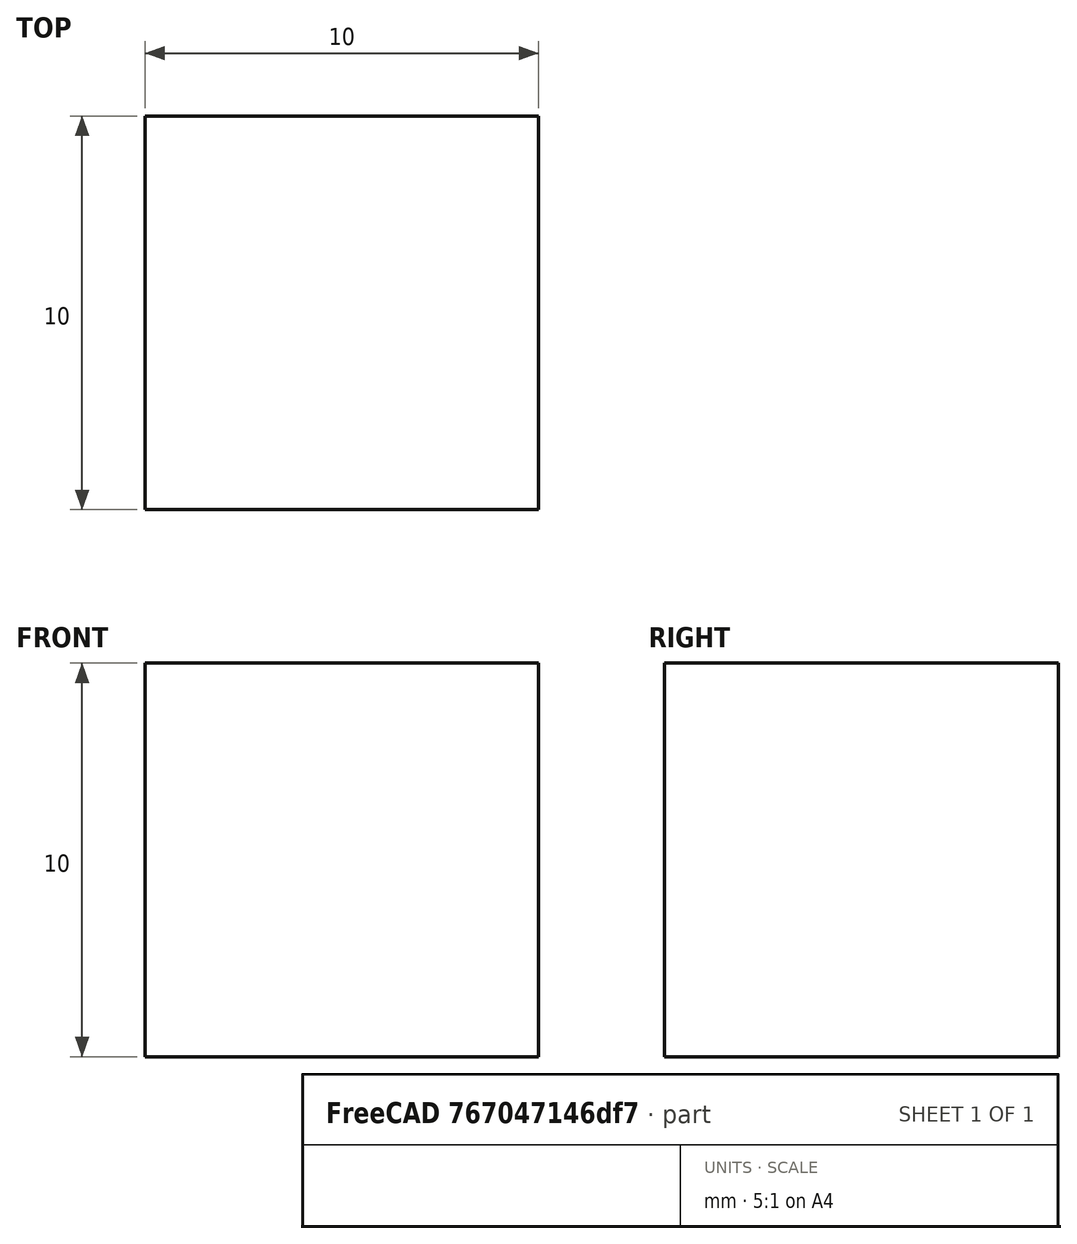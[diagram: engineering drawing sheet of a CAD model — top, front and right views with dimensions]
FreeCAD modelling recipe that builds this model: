
FCSTD DOCUMENT  (FreeCAD 0.21R33694 (Git))
Label: Block_Disp_Control_Example
License: All rights reserved
LicenseURL: http://en.wikipedia.org/wiki/All_rights_reserved
objects: Fem::ConstraintDisplacement×6, Fem::FemMeshObjectPython×2, Part::Box×1, Fem::FemSolverObjectPython×1, App::MaterialObjectPython×1, Fem::FemResultObjectPython×1, Fem::FemAnalysis×1
note: 1 computed .brp shape members not serialized (recipe doc carries the construction recipe); baked Part::Feature solids carry a one-line shape summary decoded from their .brp

FEATURE [Part::Box] Box  label="Cube"
  AttacherType = Attacher::AttachEngine3D
  Height = 10
  Length = 10
  Width = 10
FEATURE [Fem::FemSolverObjectPython] SolverCcxTools  # FEM object (typed FeaturePython)
  AnalysisType = 0
  BeamShellResultOutput3D = false
  BucklingFactors = 1
  EigenmodeHighLimit = 1000000
  EigenmodeLowLimit = 0
  EigenmodesCount = 10
  GeometricalNonlinearity = 0
  IterationsControlParameterCutb = 0.25,0.5,0.75,0.85,,,1.5,
  IterationsControlParameterIter = 4,8,9,200,10,400,,200,,
  IterationsControlParameterTimeUse = false
  IterationsThermoMechMaximum = 2000
  IterationsUserDefinedIncrementations = false
  IterationsUserDefinedTimeStepLength = false
  MaterialNonlinearity = 0
  MatrixSolverType = 0
  SplitInputWriter = false
  ThermoMechSteadyState = true
  TimeEnd = 1
  TimeInitialStep = 0.01
FEATURE [App::MaterialObjectPython] MaterialSolid  # material (typed FeaturePython)
  Category = 0
  Material = AuthorAndLicense=(c) 2013 Juergen Riegel (CC-BY 3.0),CardName=Steel-Generic,Density=7900 kg/m^3,+9 more (map truncated)
FEATURE [Fem::FemMeshObjectPython] FEMMeshGmsh  # FEM object (typed FeaturePython)
  Algorithm2D = 0
  Algorithm3D = 0
  CharacteristicLengthMax = 0
  CharacteristicLengthMin = 10
  CoherenceMesh = true
  ElementDimension = 0
  ElementOrder = 1
  GeometryTolerance = 1e-06
  GroupsOfNodes = false
  HighOrderOptimize = 0
  MeshSizeFromCurvature = 12
  OptimizeNetgen = false
  OptimizeStd = true
  Part = -> Box
  RecombinationAlgorithm = 0
  Recombine3DAll = false
  RecombineAll = false
  SecondOrderLinear = false
FEATURE [Fem::ConstraintDisplacement] ConstraintDisplacement
  NormalDirection = (0,0,-1)
  Normals = (9) [(0,0,-1),(0,0,-1),(0,0,-1),(0,0,-1),(0,0,-1),(0,0,-1),(0,0,-1),(0,0,-1),(0,0,-1)]
  Points = (9) [(0,0,0),(5,0,0),(10,0,0),(0,5,0),(5,5,0),(10,5,0),(0,10,0),(5,10,0),(10,10,0)]
  References = -> [Box]
  hasXFormula = false
  hasYFormula = false
  hasZFormula = false
  rotxFix = false
  rotxFree = true
  rotyFix = false
  rotyFree = true
  rotzFix = false
  rotzFree = true
  useFlowSurfaceForce = false
  xDisplacement = 0
  xFix = false
  xFree = true
  xRotation = 0
  yDisplacement = 0
  yFix = false
  yFree = true
  yRotation = 0
  zDisplacement = 0
  zFix = false
  zFree = false
  zRotation = 0
FEATURE [Fem::ConstraintDisplacement] ConstraintDisplacement001
  NormalDirection = (-1,0,0)
  Normals = (9) [(-1,0,0),(-1,0,0),(-1,0,0),(-1,0,0),(-1,0,0),(-1,0,0),(-1,0,0),(-1,0,0),(-1,0,0)]
  Points = (9) [(0,10,0),(0,10,5),(0,10,10),(0,5,0),(0,5,5),(0,5,10),(0,0,0),(0,0,5),(0,0,10)]
  References = -> [Box]
  hasXFormula = false
  hasYFormula = false
  hasZFormula = false
  rotxFix = false
  rotxFree = true
  rotyFix = false
  rotyFree = true
  rotzFix = false
  rotzFree = true
  useFlowSurfaceForce = false
  xDisplacement = 0
  xFix = false
  xFree = false
  xRotation = 0
  yDisplacement = 0
  yFix = false
  yFree = true
  yRotation = 0
  zDisplacement = 0
  zFix = false
  zFree = true
  zRotation = 0
FEATURE [Fem::ConstraintDisplacement] ConstraintDisplacement002
  NormalDirection = (0,1,0)
  Normals = (9) [(0,1,0),(0,1,0),(0,1,0),(0,1,0),(0,1,0),(0,1,0),(0,1,0),(0,1,0),(0,1,0)]
  Points = (9) [(0,10,0),(0,10,5),(0,10,10),(5,10,0),(5,10,5),(5,10,10),(10,10,0),(10,10,5),(10,10,10)]
  References = -> [Box]
  hasXFormula = false
  hasYFormula = false
  hasZFormula = false
  rotxFix = false
  rotxFree = true
  rotyFix = false
  rotyFree = true
  rotzFix = false
  rotzFree = true
  useFlowSurfaceForce = false
  xDisplacement = 0
  xFix = false
  xFree = true
  xRotation = 0
  yDisplacement = 0
  yFix = false
  yFree = false
  yRotation = 0
  zDisplacement = 0
  zFix = false
  zFree = true
  zRotation = 0
FEATURE [Fem::ConstraintDisplacement] ConstraintDisplacement003
  NormalDirection = (0,0,1)
  Normals = (9) [(0,0,1),(0,0,1),(0,0,1),(0,0,1),(0,0,1),(0,0,1),(0,0,1),(0,0,1),(0,0,1)]
  Points = (9) [(0,0,10),(5,0,10),(10,0,10),(0,5,10),(5,5,10),(10,5,10),(0,10,10),(5,10,10),(10,10,10)]
  References = -> [Box]
  hasXFormula = false
  hasYFormula = false
  hasZFormula = false
  rotxFix = false
  rotxFree = true
  rotyFix = false
  rotyFree = true
  rotzFix = false
  rotzFree = true
  useFlowSurfaceForce = false
  xDisplacement = 0
  xFix = false
  xFree = true
  xRotation = 0
  yDisplacement = 0
  yFix = false
  yFree = true
  yRotation = 0
  zDisplacement = 0.1
  zFix = false
  zFree = false
  zRotation = 0
FEATURE [Fem::ConstraintDisplacement] ConstraintDisplacement004
  NormalDirection = (1,0,0)
  Normals = (9) [(1,0,0),(1,0,0),(1,0,0),(1,0,0),(1,0,0),(1,0,0),(1,0,0),(1,0,0),(1,0,0)]
  Points = (9) [(10,10,0),(10,10,5),(10,10,10),(10,5,0),(10,5,5),(10,5,10),(10,0,0),(10,0,5),(10,0,10)]
  References = -> [Box]
  hasXFormula = false
  hasYFormula = false
  hasZFormula = false
  rotxFix = false
  rotxFree = true
  rotyFix = false
  rotyFree = true
  rotzFix = false
  rotzFree = true
  useFlowSurfaceForce = false
  xDisplacement = 0.01
  xFix = false
  xFree = false
  xRotation = 0
  yDisplacement = 0
  yFix = false
  yFree = true
  yRotation = 0
  zDisplacement = 0
  zFix = false
  zFree = true
  zRotation = 0
FEATURE [Fem::ConstraintDisplacement] ConstraintDisplacement005
  NormalDirection = (0,-1,0)
  Normals = (9) [(0,-1,0),(0,-1,0),(0,-1,0),(0,-1,0),(0,-1,0),(0,-1,0),(0,-1,0),(0,-1,0),(0,-1,0)]
  Points = (9) [(0,0,0),(0,0,5),(0,0,10),(5,0,0),(5,0,5),(5,0,10),(10,0,0),(10,0,5),(10,0,10)]
  References = -> [Box]
  hasXFormula = false
  hasYFormula = false
  hasZFormula = false
  rotxFix = false
  rotxFree = true
  rotyFix = false
  rotyFree = true
  rotzFix = false
  rotzFree = true
  useFlowSurfaceForce = false
  xDisplacement = 0
  xFix = false
  xFree = true
  xRotation = 0
  yDisplacement = -0.01
  yFix = false
  yFree = false
  yRotation = 0
  zDisplacement = 0
  zFix = false
  zFree = true
  zRotation = 0
FEATURE [Fem::FemMeshObjectPython] Result_Mesh_Volume  # FEM object (typed FeaturePython)
FEATURE [Fem::FemResultObjectPython] ResultMechanical  # FEM object (typed FeaturePython)
  CriticalStrainRatio = [1728.93,1728.93,1728.93,1728.93,1728.93,1728.93,1728.93,1728.93,1728.93,1728.93,1728.93,1728.93,1728.93,1728.93,1728.93,1728.93,1728.93,1728.93,1728.93,1728.93,1728.93,1728.93,1728.93,1728.93,1728.93,1728.93,1728.93,1728.93,1728.93,1728.93,+33 more]
  DisplacementLengths = [0.521763,0.0519174,0.519174,0,0.52434,0.0734222,0.521763,0.0519174,0.264728,0.519822,0.259587,0.0259587,0.269771,0.522408,0.264728,0.0580454,0.0580454,0.522408,0.0259587,0.519822,0.260882,0.391322,0.135508,0.389596,0.130441,0.265997,+37 more]
  DisplacementVectors = (63) [(0,-0.0519174,0.519174),(0,-0.0519174,0),(0,0,0.519174),(0,0,0),(0.0519174,-0.0519174,0.519174),(0.0519174,-0.0519174,0),(0.0519174,0,0.519174),+56 more]
  Eigenmode = 0
  EigenmodeFrequency = 0
  Mesh = -> Result_Mesh_Volume
  NodeNumbers = [1,2,3,4,5,6,7,8,9,10,11,12,13,14,15,16,17,18,19,20,21,22,23,24,25,26,27,28,29,30,31,32,33,34,35,36,37,38,39,40,41,42,43,44,45,46,47,48,49,50,51,52,53,54,55,56,57,58,59,60,61,62,63]
  NodeStressXX = [1526.21,1526.21,1526.21,1526.21,1526.21,1526.21,1526.21,1526.21,1526.21,1526.21,1526.21,1526.21,1526.21,1526.21,1526.21,1526.21,1526.21,1526.21,1526.21,1526.21,1526.21,1526.21,1526.21,1526.21,1526.21,1526.21,1526.21,1526.21,1526.21,1526.21,+33 more]
  NodeStressXY = [-2.40836e-12,2.43909e-12,-2.02569e-12,-3.03438e-12,-1.30272e-12,-2.64585e-12,1.82051e-12,3.15597e-12,1.53669e-14,-2.21702e-12,-2.53003e-12,-2.97645e-13,-1.97428e-12,2.58896e-13,2.48824e-12,2.55062e-13,-1.03377e-13,-1.85554e-12,6.0794e-14,+44 more]
  NodeStressXZ = [-1.35346e-11,-2.67087e-12,5.81377e-12,-6.79306e-12,8.92134e-12,9.37934e-13,-6.41394e-12,1.11667e-11,-8.10273e-12,-3.86041e-12,-4.89641e-13,-4.73196e-12,4.92964e-12,1.2537e-12,2.37636e-12,6.0523e-12,-8.66469e-13,-2.30662e-12,2.1868e-12,+44 more]
  NodeStressYY = [1526.21,1526.21,1526.21,1526.21,1526.21,1526.21,1526.21,1526.21,1526.21,1526.21,1526.21,1526.21,1526.21,1526.21,1526.21,1526.21,1526.21,1526.21,1526.21,1526.21,1526.21,1526.21,1526.21,1526.21,1526.21,1526.21,1526.21,1526.21,1526.21,1526.21,+33 more]
  NodeStressYZ = [-1.56677e-11,-2.48802e-11,-1.50031e-11,-2.09902e-11,-3.2508e-11,-4.68106e-12,-1.52833e-11,1.36869e-13,-2.0274e-11,-1.53354e-11,-1.79967e-11,-2.29352e-11,-1.85945e-11,-2.38956e-11,-7.5732e-12,-2.2721e-12,-1.47806e-11,-2.40879e-11,+45 more]
  NodeStressZZ = [100,100,100,100,100,100,100,100,100,100,100,100,100,100,100,100,100,100,100,100,100,100,100,100,100,100,100,100,100,100,100,100,100,100,100,100,100,100,100,100,100,100,100,100,100,100,100,100,100,100,100,100,100,100,100,100,100,100,100,100,+3 more]
  Peeq = [0.00928729,0.00928729,0.00928729,0.00928729,0.00928729,0.00928729,0.00928729,0.00928729,0.00928729,0.00928729,0.00928729,0.00928729,0.00928729,0.00928729,0.00928729,0.00928729,0.00928729,0.00928729,0.00928729,0.00928729,0.00928729,+42 more]
  ResultType = Fem::ResultMechanical
  Stats = [0,0.0519174,-0.0519174,0,0,0.519174,0,0.52434,1426.21,1426.21,0,0,0,0,0,0,0,0,0.00928729,0.00928729,1728.93,1728.93,0,0,0,0]
  Temperature = [1728.93,1728.93,1728.93,1728.93,1728.93,1728.93,1728.93,1728.93,1728.93,1728.93,1728.93,1728.93,1728.93,1728.93,1728.93,1728.93,1728.93,1728.93,1728.93,1728.93,1728.93,1728.93,1728.93,1728.93,1728.93,1728.93,1728.93,1728.93,1728.93,1728.93,+33 more]
  Time = 0
  vonMises = [1426.21,1426.21,1426.21,1426.21,1426.21,1426.21,1426.21,1426.21,1426.21,1426.21,1426.21,1426.21,1426.21,1426.21,1426.21,1426.21,1426.21,1426.21,1426.21,1426.21,1426.21,1426.21,1426.21,1426.21,1426.21,1426.21,1426.21,1426.21,1426.21,1426.21,+33 more]
FEATURE [Fem::FemAnalysis] Analysis
  Group = -> [SolverCcxTools,MaterialSolid,FEMMeshGmsh,ConstraintDisplacement,ConstraintDisplacement001,ConstraintDisplacement002,ConstraintDisplacement003,ConstraintDisplacement004,ConstraintDisplacement005,ResultMechanical]
